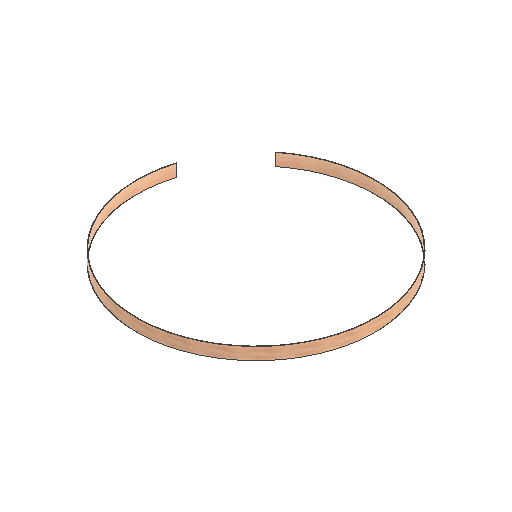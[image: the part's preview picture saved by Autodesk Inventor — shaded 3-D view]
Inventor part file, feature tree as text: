
AUTODESK INVENTOR PART (.ipt)
format: ipt  version: 2021 (Build 250183000, 183)  size: 118,784 bytes
history: native  units: mm
features: other x4, extrude x2, sketch x2, reference x2
ambient origin geometry x8: Origin, YZ Plane, XZ Plane, XY Plane, X Axis, Y Axis, Z Axis, Center Point
bodies: Solid1 (feature_tree)
feature tree (10):
  extrude  "Extrusion1"  Depth=1934.5mm
  extrude  "Extrusion2"  Depth=100.0mm TaperAngle=0.0deg
  sketch  "Sketch1"  dims[d0=1942.5mm d1=1934.5mm]
  sketch  "Sketch2"  dims[d2=100.0mm d3=0.0mm d4=100.0mm d5=0.0mm]
  reference  "Reference1"
  reference  "Reference2"
  other  "Full Scale Assembly.iam"
  other  "Disk D Assembly:1"
  other  "Platform D4:1"
  other  "Platform D1:1"
